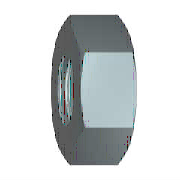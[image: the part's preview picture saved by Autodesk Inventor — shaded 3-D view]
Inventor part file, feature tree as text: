
AUTODESK INVENTOR PART (.ipt)
format: ipt  version: 2013 (Build 170138000, 138)  size: 172,032 bytes
history: native  units: mm (DEFAULTED — no unit token found)
features: sketch x3, chamfer x1, hole x1, other x1, plane x1
ambient origin geometry x7: Origin, YZ Plane, XZ Plane, X Axis, Y Axis, Z Axis, Center Point
bodies: Solid1 (feature_tree), Body (feature_tree)
feature tree (7):
  chamfer  "Chamfer1"  Distance=4.363323mm
  hole  "Thread"  [1 undecoded]
  other  "Work Axis1"
  plane  "Work Plane1"
  sketch  "Sketch1"  dims[d0=8.082904mm]
  sketch  "Sketch2"  dims[d1=3.2mm]
  sketch  "Sketch3"  dims[d2=0.0mm d3=4.363323mm d4=4.363323mm d5=7.0mm d6=7.0mm d7=90.0deg d25=3.242mm d26=6.0mm d27=4.0mm d28=2.0mm d29=14.3117mm d30=8.0mm d31=20.594885mm d8=0.378886mm d9=30.0deg d10=0.378886mm d11=30.0deg d13=0.0mm d14=0.0mm d39=0.0mm d40=0.378886mm d41=0.378886mm d42=0.0mm]
note: 1 required parameter value undecoded (feature->parameter linkage not recoverable at this tier; creation-order binding heuristic only, values carry confidence <= 0.55)
